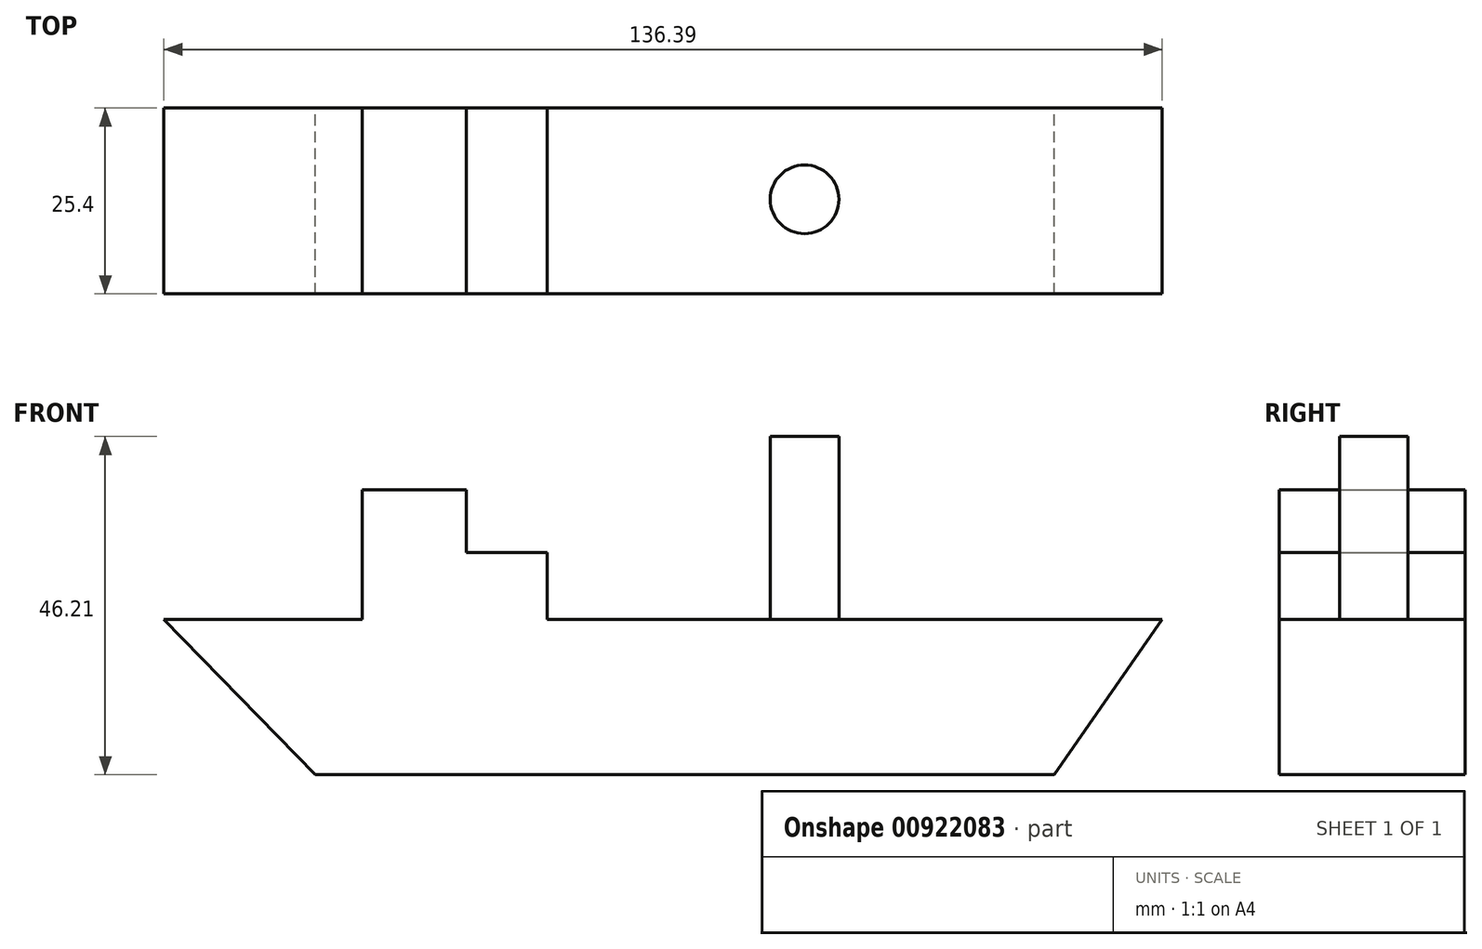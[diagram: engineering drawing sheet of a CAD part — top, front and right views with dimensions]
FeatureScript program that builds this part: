
annotation { "Feature Type Name" : "Feature", "Feature Type Description" : "" }
export const myFeature = defineFeature(function(context is Context, id is Id, definition is map)
    precondition{}
    {
        {
            var Q0;
            Q0=qCreatedBy(makeId("Front.planeOp"),FACE);
            var sketch = newSketch(context, id + "F0", { "sketchPlane" : qUnion([Q0])});
            skLineSegment(sketch, "E0", {"start": v(-73.97, -26.18) * mm, "end": v(-53.3, -47.39) * mm});
            skLineSegment(sketch, "E1", {"start": v(-53.3, -47.39) * mm, "end": v(47.66, -47.39) * mm});
            skLineSegment(sketch, "E2", {"start": v(-73.97, -26.18) * mm, "end": v(-46.85, -26.18) * mm});
            skLineSegment(sketch, "E3", {"start": v(-46.85, -8.46) * mm, "end": v(-46.85, -26.18) * mm});
            skLineSegment(sketch, "E4", {"start": v(-46.85, -8.46) * mm, "end": v(-32.62, -8.46) * mm});
            skLineSegment(sketch, "E5", {"start": v(-32.62, -8.46) * mm, "end": v(-32.62, -17.05) * mm});
            skLineSegment(sketch, "E6", {"start": v(-32.62, -17.05) * mm, "end": v(-21.61, -17.05) * mm});
            skLineSegment(sketch, "E7", {"start": v(-21.61, -17.05) * mm, "end": v(-21.61, -26.18) * mm});
            skLineSegment(sketch, "E8", {"start": v(-46.85, -26.18) * mm, "end": v(-21.61, -26.18) * mm});
            skLineSegment(sketch, "E9", {"start": v(-21.61, -26.18) * mm, "end": v(0, -26.18) * mm});
            skLineSegment(sketch, "E10", {"start": v(0, -26.18) * mm, "end": v(13.3, -26.18) * mm});
            skLineSegment(sketch, "E11", {"start": v(13.3, -26.18) * mm, "end": v(62.42, -26.18) * mm});
            skLineSegment(sketch, "E12", {"start": v(62.42, -26.18) * mm, "end": v(47.66, -47.39) * mm});
            skSolve(sketch);
        }
        {
            var Q0;
            Q0 = qSketchRegion(id + "F0", true);
            extrude(context, id + "F1", {"entities" : qUnion([Q0]), "depth" : 25.4 * mm, "offsetDistance" : 25.4 * mm});
        }
        {
            var Q0;
            Q0=makeQuery(id+"F1.opExtrude","SWEPT_FACE",FACE,{"disambiguationData":[OSD([sQuery(id+"F0.wireOp",EDGE,"E9"),sQuery(id+"F0.wireOp",EDGE,"E10"),sQuery(id+"F0.wireOp",EDGE,"E11")])]});
            var sketch = newSketch(context, id + "F2", { "sketchPlane" : qUnion([Q0])});
            skCircle(sketch, "E13", {"center": v(13.56, -12.48) * mm, "radius": 4.69 * mm});
            skSolve(sketch);
        }
        {
            var Q0;
            Q0=makeQuery(id+"F1.opExtrude","CAP_FACE",FACE,{"disambiguationData":[OSD([sQuery(id+"F0.wireOp",EDGE,"E0"),sQuery(id+"F0.wireOp",EDGE,"E1"),sQuery(id+"F0.wireOp",EDGE,"E2"),sQuery(id+"F0.wireOp",EDGE,"E3"),sQuery(id+"F0.wireOp",EDGE,"E4"),sQuery(id+"F0.wireOp",EDGE,"E5"),sQuery(id+"F0.wireOp",EDGE,"E6"),sQuery(id+"F0.wireOp",EDGE,"E7"),sQuery(id+"F0.wireOp",EDGE,"E9"),sQuery(id+"F0.wireOp",EDGE,"E10"),sQuery(id+"F0.wireOp",EDGE,"E11"),sQuery(id+"F0.wireOp",EDGE,"E12")])],"isStart":false});
            var sketch = newSketch(context, id + "F3", { "sketchPlane" : qUnion([Q0])});
            skSolve(sketch);
        }
        {
            var Q0;
            Q0 = qSketchRegion(id + "F3", true);
            var Q1;
            Q1=makeQuery(id+"F2.imprint","IMPRINT",FACE,{"disambiguationData":[TD([[makeQuery(id+"F2.imprint","IMPRINT",EDGE,{"derivedFrom":sQuery(id+"F2.wireOp",EDGE,"E13")}),1.0]])]});
            extrude(context, id + "F4", {"entities" : qUnion([Q0, Q1]), "operationType" : NewBodyOperationType.ADD, "depth" : 25 * mm, "offsetDistance" : 25 * mm});
        }
    });
